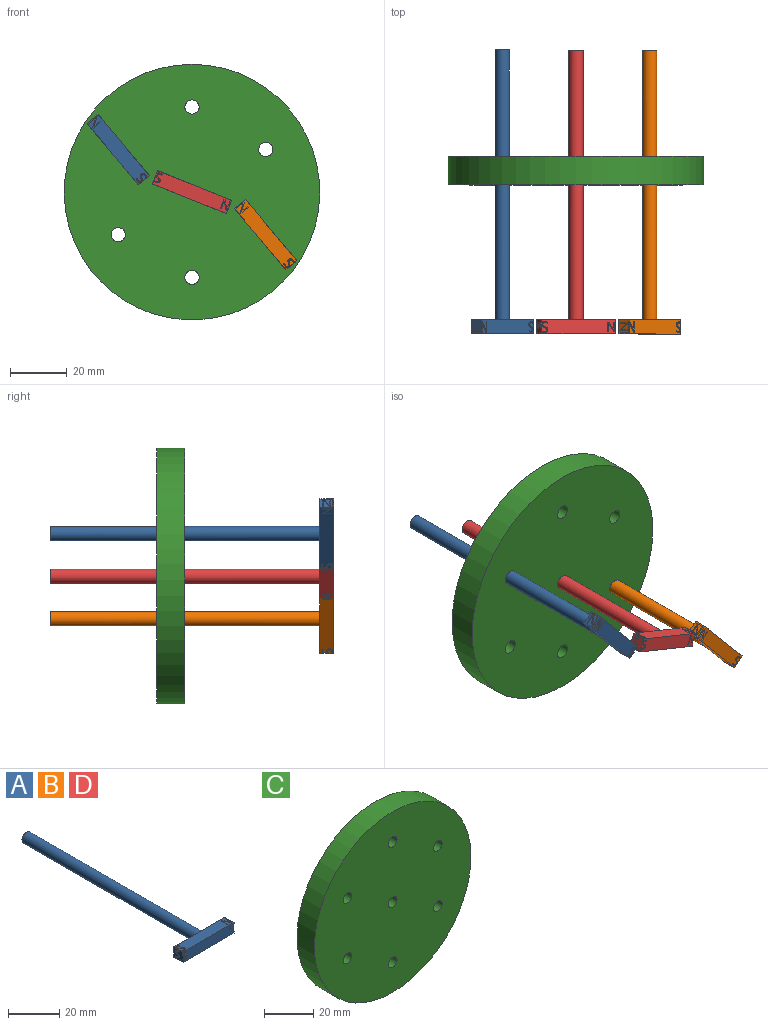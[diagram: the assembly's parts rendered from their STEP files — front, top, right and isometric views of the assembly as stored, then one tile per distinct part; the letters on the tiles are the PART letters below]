
ASSEMBLY  parts=4 mates=3
PART A: 175 faces, bbox 28x100x5 mm
  f0: plane 5x5mm, normal (-1,0,0), area 21.3mm2, adj f2,f3,f4,f5,f6,f9,f11,f12
  f1: plane 5x5mm, normal (1,0,0), area 16.9mm2, adj f2,f4,f5,f10,f52,f53,f54,f93
  f2: plane 28.02x5mm, normal (0,-1,0), area 131.4mm2, adj f0,f1,f4,f5,f93,f94,f96,f97
  f3: plane 2.09x1.7mm, normal (0,-1,0), area 2.1mm2, adj f0,f111,f112,f126,f127,f128,f129,f130
  f4: plane 28x5mm, normal (0,0,-1), area 133.6mm2, adj f0,f1,f2,f9,f10,f52,f53,f55
  f5: plane 28.02x5mm, normal (0,0,1), area 130.5mm2, adj f0,f1,f2,f9,f10,f11,f12,f16
  f6: plane 2.07x1.79mm, normal (0,0,1), area 2.4mm2, adj f0,f13,f14,f29,f30,f31,f32,f33
  f7: cylinder r=2.5mm len=95mm, axis (0,-1,0), area 1492.3mm2, adj f8,f9,f10
  f8: plane 5x5mm, normal (0,1,0), area 19.6mm2, adj f7
  f9: plane 14x5mm, normal (0,1,0), area 60.2mm2, adj f0,f4,f5,f7
  f10: plane 14x5mm, normal (0,1,0), area 60.2mm2, adj f1,f4,f5,f7
  f11: extruded ~0.89x0.5mm, area 0.4mm2, adj f0,f5,f15,f16
  f12: extruded ~0.5x0.26mm, area 0.2mm2, adj f0,f5,f15,f28
  f13: extruded ~0.5x0.18mm, area 0.1mm2, adj f0,f6,f15,f29
  f14: extruded ~0.5x0.35mm, area 0.2mm2, adj f0,f6,f15,f35
  f15: plane 3.91x2.26mm, normal (0,0,1), area 3.2mm2, adj f0,f11,f12,f13,f14,f16,f17,f18
  f16: extruded ~0.99x0.5mm, area 0.5mm2, adj f5,f11,f15,f17
  f17: extruded ~0.78x0.5mm, area 0.4mm2, adj f5,f15,f16,f18
  f18: extruded ~0.64x0.5mm, area 0.3mm2, adj f5,f15,f17,f19
  f19: extruded ~0.82x0.5mm, area 0.5mm2, adj f5,f15,f18,f20
  f20: extruded ~0.53x0.5mm, area 0.3mm2, adj f5,f15,f19,f21
  f21: extruded ~0.5x0.25mm, area 0.2mm2, adj f5,f15,f20,f22
  f22: extruded ~0.5x0.32mm, area 0.2mm2, adj f5,f15,f21,f23
  f23: extruded ~0.5x0.42mm, area 0.2mm2, adj f5,f15,f22,f24
  f24: extruded ~0.55x0.5mm, area 0.3mm2, adj f5,f15,f23,f25
  f25: extruded ~0.92x0.5mm, area 0.5mm2, adj f5,f15,f24,f26
  f26: plane 0.5x0.39mm, normal (-0.94,0.34,0), area 0.2mm2, adj f5,f15,f25,f27
  f27: extruded ~1.04x0.5mm, area 0.5mm2, adj f5,f15,f26,f28
  f28: extruded ~0.88x0.5mm, area 0.5mm2, adj f5,f12,f15,f27
  f29: extruded ~0.76x0.5mm, area 0.4mm2, adj f6,f13,f15,f30
  f30: extruded ~0.57x0.5mm, area 0.3mm2, adj f6,f15,f29,f31
  f31: extruded ~0.5x0.27mm, area 0.2mm2, adj f6,f15,f30,f32
  f32: extruded ~0.5x0.32mm, area 0.2mm2, adj f6,f15,f31,f33
  f33: extruded ~0.5x0.47mm, area 0.3mm2, adj f6,f15,f32,f34
  f34: extruded ~0.67x0.5mm, area 0.3mm2, adj f6,f15,f33,f35
  f35: extruded ~0.55x0.5mm, area 0.3mm2, adj f6,f14,f15,f34
  f36: plane 0.5x0.45mm, normal (0,1,0), area 0.2mm2, adj f5,f37,f50,f51
  f37: plane 3.4x0.5mm, normal (-1,0,0), area 1.7mm2, adj f5,f36,f38,f51
  f38: plane 0.5x0.37mm, normal (0,-1,0), area 0.2mm2, adj f5,f37,f39,f51
  f39: plane 1.95x0.5mm, normal (1,0,0), area 1mm2, adj f5,f38,f40,f51
  f40: extruded ~0.5x0.49mm, area 0.2mm2, adj f5,f39,f41,f51
  f41: extruded ~0.5x0.4mm, area 0.2mm2, adj f5,f40,f42,f51
  f42: plane 0.5x0.02mm, normal (0,-1,0), area 0mm2, adj f5,f41,f43,f51
  f43: plane 2.84x1.85mm, normal (-0.84,-0.55,0), area 1.7mm2, adj f5,f42,f44,f51
  f44: plane 0.5x0.45mm, normal (0,-1,0), area 0.2mm2, adj f5,f43,f45,f51
  f45: plane 3.4x0.5mm, normal (1,0,0), area 1.7mm2, adj f5,f44,f46,f51
  f46: plane 0.5x0.37mm, normal (0,1,0), area 0.2mm2, adj f5,f45,f47,f51
  f47: plane 1.93x0.5mm, normal (-1,0,0), area 1mm2, adj f5,f46,f48,f51
  f48: extruded ~0.92x0.5mm, area 0.5mm2, adj f5,f47,f49,f51
  f49: plane 0.5x0.02mm, normal (0,1,0), area 0mm2, adj f5,f48,f50,f51
  f50: plane 2.85x1.86mm, normal (0.84,0.55,0), area 1.7mm2, adj f5,f36,f49,f51
  f51: plane 3.4x2.66mm, normal (0,0,1), area 3.8mm2, adj f36,f37,f38,f39,f40,f41,f42,f43
  f52: plane 0.5x0.15mm, normal (0,-1,0), area 0.1mm2, adj f1,f4,f54,f66
  f53: plane 0.5x0.06mm, normal (0,1,0), area 0mm2, adj f1,f4,f54,f55
  f54: plane 3.79x2.6mm, normal (0,0,-1), area 3.4mm2, adj f1,f52,f53,f55,f56,f57,f58,f59
  f55: plane 2.18x0.5mm, normal (1,0,0), area 1.1mm2, adj f4,f53,f54,f56
  f56: extruded ~0.54x0.5mm, area 0.3mm2, adj f4,f54,f55,f57
  f57: extruded ~0.5x0.45mm, area 0.2mm2, adj f4,f54,f56,f58
  f58: plane 0.5x0.02mm, normal (0,1,0), area 0mm2, adj f4,f54,f57,f59
  f59: plane 3.17x2.07mm, normal (-0.84,0.55,0), area 1.9mm2, adj f4,f54,f58,f60
  f60: plane 0.5x0.5mm, normal (0,1,0), area 0.2mm2, adj f4,f54,f59,f61
  f61: plane 3.79x0.5mm, normal (1,0,0), area 1.9mm2, adj f4,f54,f60,f62
  f62: plane 0.5x0.41mm, normal (0,-1,0), area 0.2mm2, adj f4,f54,f61,f63
  f63: plane 2.15x0.5mm, normal (-1,0,0), area 1.1mm2, adj f4,f54,f62,f64
  f64: extruded ~1.03x0.5mm, area 0.5mm2, adj f4,f54,f63,f65
  f65: plane 0.5x0.02mm, normal (0,-1,0), area 0mm2, adj f4,f54,f64,f66
  f66: plane 3.18x2.07mm, normal (0.84,-0.55,0), area 1.9mm2, adj f4,f52,f54,f65
  f67: extruded ~0.74x0.5mm, area 0.4mm2, adj f4,f68,f91,f92
  f68: extruded ~0.6x0.5mm, area 0.3mm2, adj f4,f67,f69,f92
  f69: extruded ~0.78x0.5mm, area 0.4mm2, adj f4,f68,f70,f92
  f70: extruded ~0.5x0.5mm, area 0.3mm2, adj f4,f69,f71,f92
  f71: extruded ~0.5x0.23mm, area 0.2mm2, adj f4,f70,f72,f92
  f72: extruded ~0.5x0.31mm, area 0.2mm2, adj f4,f71,f73,f92
  f73: extruded ~0.5x0.39mm, area 0.2mm2, adj f4,f72,f74,f92
  f74: extruded ~0.52x0.5mm, area 0.3mm2, adj f4,f73,f75,f92
  f75: extruded ~0.86x0.5mm, area 0.4mm2, adj f4,f74,f76,f92
  f76: plane 0.5x0.36mm, normal (-0.94,-0.34,0), area 0.2mm2, adj f4,f75,f77,f92
  f77: extruded ~0.98x0.5mm, area 0.5mm2, adj f4,f76,f78,f92
  f78: extruded ~0.82x0.5mm, area 0.4mm2, adj f4,f77,f79,f92
  f79: extruded ~0.66x0.5mm, area 0.4mm2, adj f4,f78,f80,f92
  f80: extruded ~0.64x0.5mm, area 0.3mm2, adj f4,f79,f81,f92
  f81: extruded ~0.71x0.5mm, area 0.4mm2, adj f4,f80,f82,f92
  f82: extruded ~0.53x0.5mm, area 0.3mm2, adj f4,f81,f83,f92
  f83: extruded ~0.5x0.25mm, area 0.2mm2, adj f4,f82,f84,f92
  f84: extruded ~0.5x0.3mm, area 0.2mm2, adj f4,f83,f85,f92
  f85: extruded ~0.5x0.44mm, area 0.3mm2, adj f4,f84,f86,f92
  f86: extruded ~0.63x0.5mm, area 0.3mm2, adj f4,f85,f87,f92
  f87: extruded ~0.51x0.5mm, area 0.3mm2, adj f4,f86,f88,f92
  f88: extruded ~0.5x0.48mm, area 0.3mm2, adj f4,f87,f89,f92
  f89: plane 0.5x0.4mm, normal (1,0,0), area 0.2mm2, adj f4,f88,f90,f92
  f90: extruded ~0.98x0.5mm, area 0.5mm2, adj f4,f89,f91,f92
  f91: extruded ~0.93x0.5mm, area 0.5mm2, adj f4,f67,f90,f92
  f92: plane 3.68x2.25mm, normal (0,0,-1), area 3mm2, adj f67,f68,f69,f70,f71,f72,f73,f74
  f93: plane 0.5x0.42mm, normal (0,0,1), area 0.2mm2, adj f1,f2,f95,f96
  f94: plane 0.5x0.33mm, normal (0,0,-1), area 0.2mm2, adj f1,f2,f95,f97
  f95: plane 3.44x2.65mm, normal (0,-1,0), area 3.8mm2, adj f1,f93,f94,f96,f97,f98,f99,f100
  f96: plane 2.89x1.88mm, normal (0.84,0,0.55), area 1.7mm2, adj f2,f93,f95,f107
  f97: plane 1.98x0.5mm, normal (1,0,0), area 1mm2, adj f2,f94,f95,f98
  f98: extruded ~0.5x0.49mm, area 0.2mm2, adj f2,f95,f97,f99
  f99: extruded ~0.5x0.41mm, area 0.2mm2, adj f2,f95,f98,f100
  f100: plane 0.5x0.02mm, normal (0,0,-1), area 0mm2, adj f2,f95,f99,f101
  f101: plane 2.88x1.88mm, normal (-0.84,0,-0.55), area 1.7mm2, adj f2,f95,f100,f102
  f102: plane 0.5x0.45mm, normal (0,0,-1), area 0.2mm2, adj f2,f95,f101,f103
  f103: plane 3.44x0.5mm, normal (1,0,0), area 1.7mm2, adj f2,f95,f102,f104
  f104: plane 0.5x0.37mm, normal (0,0,1), area 0.2mm2, adj f2,f95,f103,f105
  f105: plane 1.96x0.5mm, normal (-1,0,0), area 1mm2, adj f2,f95,f104,f106
  f106: extruded ~0.93x0.5mm, area 0.5mm2, adj f2,f95,f105,f107
  f107: plane 0.5x0.02mm, normal (0,0,1), area 0mm2, adj f2,f95,f96,f106
  f108: plane 3.54x2.12mm, normal (0,-1,0), area 2.7mm2, adj f0,f109,f110,f111,f112,f113,f114,f115
  f109: extruded ~0.87x0.5mm, area 0.4mm2, adj f0,f2,f108,f113
  f110: extruded ~0.5x0.42mm, area 0.3mm2, adj f0,f2,f108,f125
  f111: extruded ~0.5x0.37mm, area 0.2mm2, adj f0,f3,f108,f126
  f112: extruded ~0.5x0.39mm, area 0.2mm2, adj f0,f3,f108,f132
  f113: extruded ~0.9x0.5mm, area 0.5mm2, adj f2,f108,f109,f114
  f114: extruded ~0.71x0.5mm, area 0.4mm2, adj f2,f108,f113,f115
  f115: extruded ~0.57x0.5mm, area 0.3mm2, adj f2,f108,f114,f116
  f116: extruded ~0.75x0.5mm, area 0.4mm2, adj f2,f108,f115,f117
  f117: extruded ~0.5x0.48mm, area 0.3mm2, adj f2,f108,f116,f118
  f118: extruded ~0.5x0.22mm, area 0.2mm2, adj f2,f108,f117,f119
  f119: extruded ~0.5x0.29mm, area 0.2mm2, adj f2,f108,f118,f120
  f120: extruded ~0.5x0.38mm, area 0.2mm2, adj f2,f108,f119,f121
  f121: extruded ~0.5x0.5mm, area 0.3mm2, adj f2,f108,f120,f122
  f122: extruded ~0.83x0.5mm, area 0.4mm2, adj f2,f108,f121,f123
  f123: plane 0.5x0.35mm, normal (-0.94,0,0.34), area 0.2mm2, adj f2,f108,f122,f124
  f124: extruded ~0.94x0.5mm, area 0.5mm2, adj f2,f108,f123,f125
  f125: extruded ~0.79x0.5mm, area 0.4mm2, adj f2,f108,f110,f124
  f126: extruded ~0.69x0.5mm, area 0.4mm2, adj f3,f108,f111,f127
  f127: extruded ~0.51x0.5mm, area 0.3mm2, adj f3,f108,f126,f128
  f128: extruded ~0.5x0.24mm, area 0.2mm2, adj f3,f108,f127,f129
  f129: extruded ~0.5x0.29mm, area 0.2mm2, adj f3,f108,f128,f130
  f130: extruded ~0.5x0.42mm, area 0.2mm2, adj f3,f108,f129,f131
  f131: extruded ~0.6x0.5mm, area 0.3mm2, adj f3,f108,f130,f132
  f132: extruded ~0.5x0.49mm, area 0.2mm2, adj f3,f108,f112,f131
  f133: plane 0.5x0.49mm, normal (0,0,1), area 0.2mm2, adj f1,f134,f147,f148
  f134: plane 3.67x0.5mm, normal (0,-1,0), area 1.8mm2, adj f1,f133,f135,f148
  f135: plane 0.5x0.4mm, normal (0,0,-1), area 0.2mm2, adj f1,f134,f136,f148
  f136: plane 2.11x0.5mm, normal (0,1,0), area 1.1mm2, adj f1,f135,f137,f148
  f137: extruded ~0.53x0.5mm, area 0.3mm2, adj f1,f136,f138,f148
  f138: extruded ~0.5x0.44mm, area 0.2mm2, adj f1,f137,f139,f148
  f139: plane 0.5x0.02mm, normal (0,0,-1), area 0mm2, adj f1,f138,f140,f148
  f140: plane 3.07x2mm, normal (0,-0.84,-0.55), area 1.8mm2, adj f1,f139,f141,f148
  f141: plane 0.5x0.48mm, normal (0,0,-1), area 0.2mm2, adj f1,f140,f142,f148
  f142: plane 3.67x0.5mm, normal (0,1,0), area 1.8mm2, adj f1,f141,f143,f148
  f143: plane 0.5x0.39mm, normal (0,0,1), area 0.2mm2, adj f1,f142,f144,f148
  f144: plane 2.09x0.5mm, normal (0,-1,0), area 1mm2, adj f1,f143,f145,f148
  f145: extruded ~0.99x0.5mm, area 0.5mm2, adj f1,f144,f146,f148
  f146: plane 0.5x0.02mm, normal (0,0,1), area 0mm2, adj f1,f145,f147,f148
  f147: plane 3.08x2.01mm, normal (0,0.84,0.55), area 1.8mm2, adj f1,f133,f146,f148
  f148: plane 3.67x2.87mm, normal (1,0,0), area 4.4mm2, adj f133,f134,f135,f136,f137,f138,f139,f140
  f149: extruded ~0.69x0.5mm, area 0.4mm2, adj f0,f150,f173,f174
  f150: extruded ~0.56x0.5mm, area 0.3mm2, adj f0,f149,f151,f174
  f151: extruded ~0.73x0.5mm, area 0.4mm2, adj f0,f150,f152,f174
  f152: extruded ~0.5x0.47mm, area 0.3mm2, adj f0,f151,f153,f174
  f153: extruded ~0.5x0.22mm, area 0.2mm2, adj f0,f152,f154,f174
  f154: extruded ~0.5x0.29mm, area 0.1mm2, adj f0,f153,f155,f174
  f155: extruded ~0.5x0.37mm, area 0.2mm2, adj f0,f154,f156,f174
  f156: extruded ~0.5x0.48mm, area 0.3mm2, adj f0,f155,f157,f174
  f157: extruded ~0.81x0.5mm, area 0.4mm2, adj f0,f156,f158,f174
  f158: plane 0.5x0.34mm, normal (0,0.94,0.34), area 0.2mm2, adj f0,f157,f159,f174
  f159: extruded ~0.92x0.5mm, area 0.5mm2, adj f0,f158,f160,f174
  f160: extruded ~0.77x0.5mm, area 0.4mm2, adj f0,f159,f161,f174
  f161: extruded ~0.62x0.5mm, area 0.4mm2, adj f0,f160,f162,f174
  f162: extruded ~0.6x0.5mm, area 0.3mm2, adj f0,f161,f163,f174
  f163: extruded ~0.67x0.5mm, area 0.4mm2, adj f0,f162,f164,f174
  f164: extruded ~0.5x0.5mm, area 0.3mm2, adj f0,f163,f165,f174
  f165: extruded ~0.5x0.23mm, area 0.2mm2, adj f0,f164,f166,f174
  f166: extruded ~0.5x0.29mm, area 0.1mm2, adj f0,f165,f167,f174
  f167: extruded ~0.5x0.41mm, area 0.2mm2, adj f0,f166,f168,f174
  f168: extruded ~0.59x0.5mm, area 0.3mm2, adj f0,f167,f169,f174
  f169: extruded ~0.5x0.48mm, area 0.2mm2, adj f0,f168,f170,f174
  f170: extruded ~0.5x0.45mm, area 0.2mm2, adj f0,f169,f171,f174
  f171: plane 0.5x0.38mm, normal (0,-1,0), area 0.2mm2, adj f0,f170,f172,f174
  f172: extruded ~0.92x0.5mm, area 0.5mm2, adj f0,f171,f173,f174
  f173: extruded ~0.87x0.5mm, area 0.5mm2, adj f0,f149,f172,f174
  f174: plane 3.45x2.11mm, normal (-1,0,0), area 2.6mm2, adj f149,f150,f151,f152,f153,f154,f155,f156
PART B: same geometry as A
PART C: 10 faces, bbox 90x10x90 mm
  f0: cylinder r=2.5mm len=10mm, axis (0,1,0), area 157.1mm2, adj f8,f9
  f1: cylinder r=2.5mm len=10mm, axis (0,1,0), area 157.1mm2, adj f8,f9
  f2: cylinder r=2.5mm len=10mm, axis (0,1,0), area 157.1mm2, adj f8,f9
  f3: cylinder r=2.5mm len=10mm, axis (0,1,0), area 157.1mm2, adj f8,f9
  f4: cylinder r=2.5mm len=10mm, axis (0,1,0), area 157.1mm2, adj f8,f9
  f5: cylinder r=2.5mm len=10mm, axis (0,1,0), area 157.1mm2, adj f8,f9
  f6: cylinder r=2.5mm len=10mm, axis (0,1,0), area 157.1mm2, adj f8,f9
  f7: cylinder r=45mm len=90mm, axis (0,1,0), area 2827.4mm2, adj f8,f9
  f8: plane 90x90mm, normal (0,-1,0), area 6224.3mm2, adj f0,f1,f2,f3,f4,f5,f6,f7
  f9: plane 90x90mm, normal (0,1,0), area 6224.3mm2, adj f0,f1,f2,f3,f4,f5,f6,f7
PART D: same geometry as A
PLACE A rot(axis=(0,-1,0),130deg) t=(-28.48,-55,15.62)mm
PLACE B rot(axis=(0,-1,0),130deg) t=(23.48,-55,-14.38)mm
PLACE C rot(axis=(0,1,0),180deg) t=(-2.5,7.5,0.62)mm
PLACE D rot(axis=(0,1,0),22deg) t=(-2.5,-55,0.62)mm
MATE revolute D.f7 <-> C.f7  axis (0,-1,0) through (-2.5,-2.5,0.62)mm
MATE revolute A.f7 <-> C.f3  axis (0,-1,0) through (-28.48,-2.5,15.62)mm
MATE revolute B.f7 <-> C.f6  axis (0,-1,0) through (23.48,-2.5,-14.38)mm
